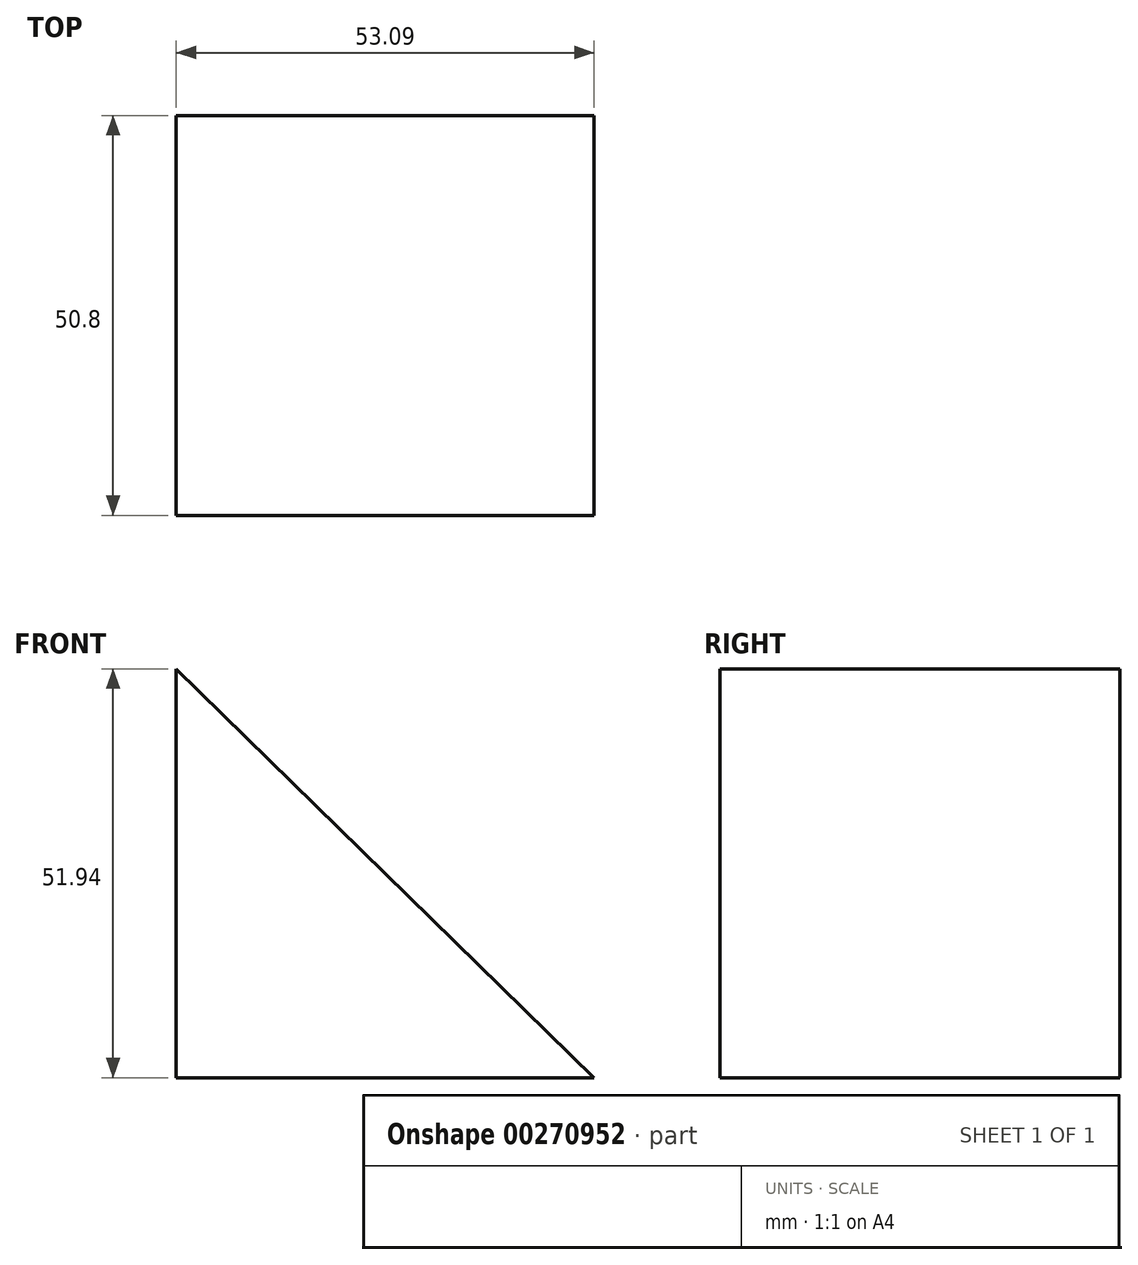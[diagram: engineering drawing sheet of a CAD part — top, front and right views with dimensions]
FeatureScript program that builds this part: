
annotation { "Feature Type Name" : "Feature", "Feature Type Description" : "" }
export const myFeature = defineFeature(function(context is Context, id is Id, definition is map)
    precondition{}
    {
        {
            var Q0;
            Q0=qCreatedBy(makeId("Front.planeOp"),FACE);
            var sketch = newSketch(context, id + "F0", { "sketchPlane" : qUnion([Q0])});
            skLineSegment(sketch, "E0", {"start": v(-53.09, 0) * mm, "end": v(-53.09, 51.94) * mm});
            skLineSegment(sketch, "E1", {"start": v(-53.09, 51.94) * mm, "end": v(0, 0) * mm});
            skLineSegment(sketch, "E2", {"start": v(0, 0) * mm, "end": v(-53.09, 0) * mm});
            skSolve(sketch);
        }
        {
            var Q0;
            Q0 = qSketchRegion(id + "F0", true);
            extrude(context, id + "F1", {"entities" : qUnion([Q0]), "depth" : 50.8 * mm});
        }
    });
